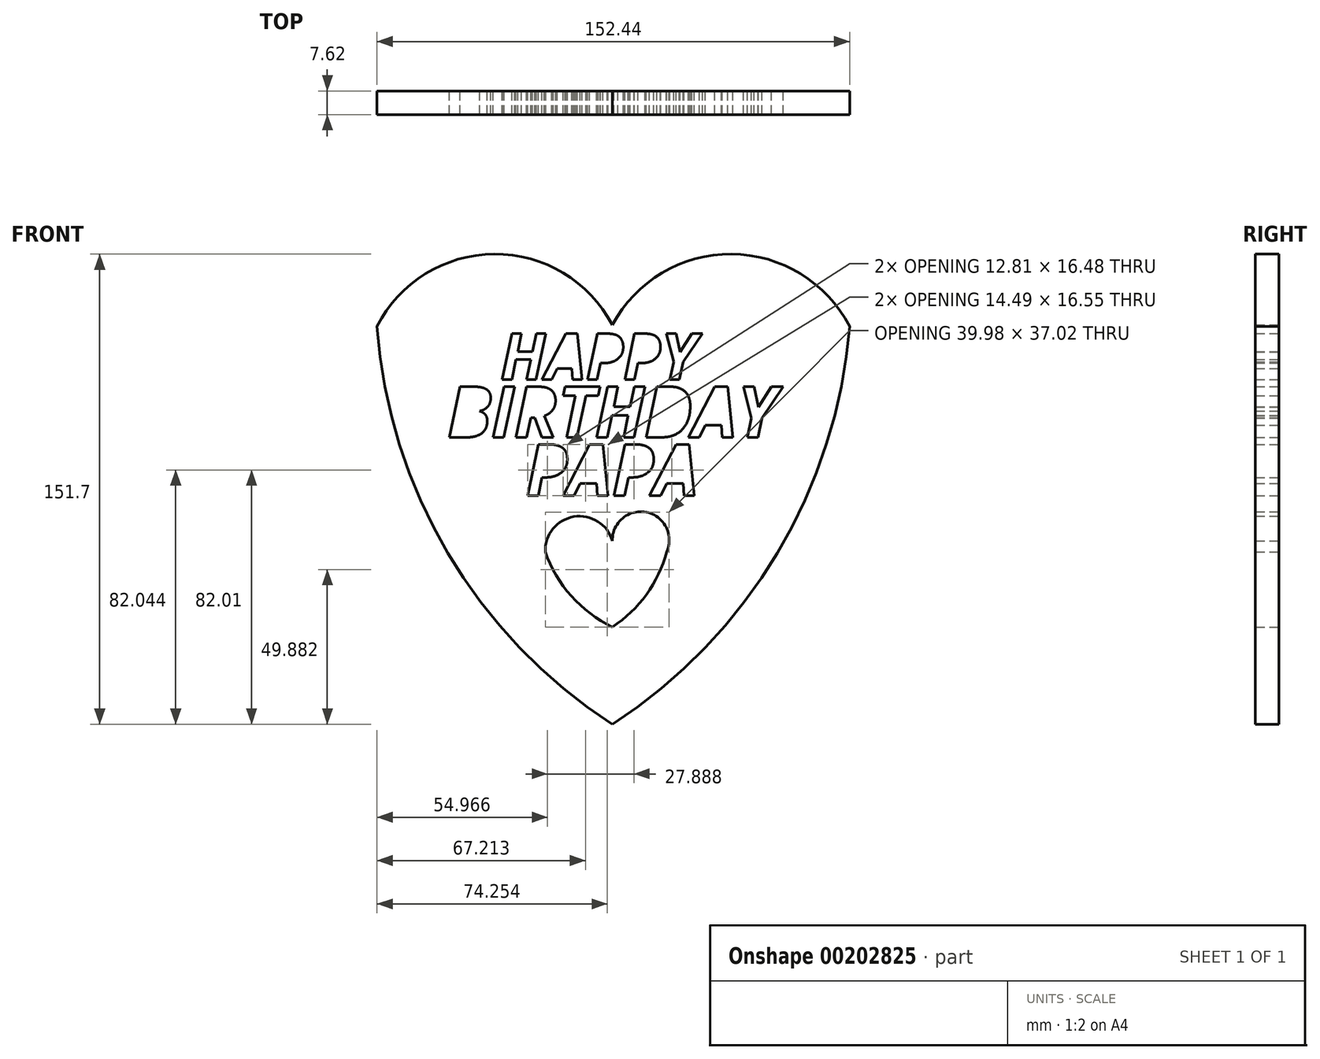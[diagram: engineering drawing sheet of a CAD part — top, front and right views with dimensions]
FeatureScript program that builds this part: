
annotation { "Feature Type Name" : "Feature", "Feature Type Description" : "" }
export const myFeature = defineFeature(function(context is Context, id is Id, definition is map)
    precondition{}
    {
        {
            var Q0;
            Q0=qCreatedBy(makeId("Front.planeOp"),FACE);
            var sketch = newSketch(context, id + "F0", { "sketchPlane" : qUnion([Q0])});
            skArc(sketch, "E0", {"start": v(0, 53.3) * mm, "mid": v(-38.1, 76.12) * mm, "end": v(-75.9, 52.79) * mm});
            skArc(sketch, "E1", {"start": v(76.54, 52.79) * mm, "mid": v(38.42, 76.12) * mm, "end": v(0, 53.3) * mm});
            skArc(sketch, "E2", {"start": v(-75.9, 52.79) * mm, "mid": v(-53.08, -20.34) * mm, "end": v(0, -75.58) * mm});
            skArc(sketch, "E3", {"start": v(0, -75.58) * mm, "mid": v(53.23, -20.32) * mm, "end": v(76.54, 52.79) * mm});
            skText(sketch, "E4", { "text": "HAPPY", "fontName": "OpenSans-BoldItalic.ttf"});
            skText(sketch, "E5", { "text": "BIRTHDAY", "fontName": "OpenSans-BoldItalic.ttf"});
            skText(sketch, "E6", { "text": "PAPA", "fontName": "OpenSans-BoldItalic.ttf"});
            skArc(sketch, "E7", {"start": v(0, -16.4) * mm, "mid": v(-12.4, -8.63) * mm, "end": v(-21.64, -19.96) * mm});
            skArc(sketch, "E8", {"start": v(17.53, -19.96) * mm, "mid": v(11, -7.19) * mm, "end": v(0, -16.4) * mm});
            skArc(sketch, "E9", {"start": v(-21.64, -19.96) * mm, "mid": v(-13.22, -34.22) * mm, "end": v(0, -44.2) * mm});
            skArc(sketch, "E10", {"start": v(0, -44.2) * mm, "mid": v(11.02, -33.71) * mm, "end": v(17.53, -19.96) * mm});
            const initialGuessF0  = {"E4": [-0.03605, 0.03566, 1, 0, 0.01492], "E5": [-0.05318, 0.017, 1, 0, 0.01645], "E6": [-0.02794, -0.00181, 1, 0, 0.01662]};
            skSetInitialGuess(sketch, initialGuessF0);
            skSolve(sketch);
        }
        {
            var Q0;
            Q0=makeQuery(id+"F0.imprint","IMPRINT",FACE,{"disambiguationData":[TD([[makeQuery(id+"F0.imprint","IMPRINT",EDGE,{"derivedFrom":sQuery(id+"F0.wireOp",EDGE,"E0")}),1.0]])]});
            extrude(context, id + "F1", {"entities" : qUnion([Q0]), "depth" : 7.62 * mm});
        }
    });
